# Revit family: Doors_Openers_Gilgen_Swing-Door-Drive-Unit-FD-10 Popravljena
name_source: partatom
category: Generic Models
revit_build: Autodesk Revit 2015 (Build: 20140606_1530(x64)
units: mm (PartAtom-declared; Revit-internal decimal feet)

## types (2) — shared parameters
Assembly Code = E10
Edition number = 1
Keynote = 08700
Manufacturer = Gilgen
Model = Door Operator FD10
Product Guid = ad6d4fb3-5188-4a42-9f31-05ed5f2be77f
Product data url = https://bimobject.com
URL = https://www.gilgendoorsystems.com
zero-valued in all types: Default Elevation

## per-type parameters (varying)
| type | Product Material | Type Comments |
| Operator FD10 - Aluminium | Metal - Gilgen - Aluminium Satin | Gilgen Door Operator FD10, with aluminium covering |
| Operator FD10 - Stainless Steel | Metal - Gilgen - Stainless Steel Polished | Gilgen Door Operator FD10, with stainless steel covering |

## geometry (parser evidence)
native form markers: Blend x2, Sweep x23
no freeform markers — native parametric forms only
